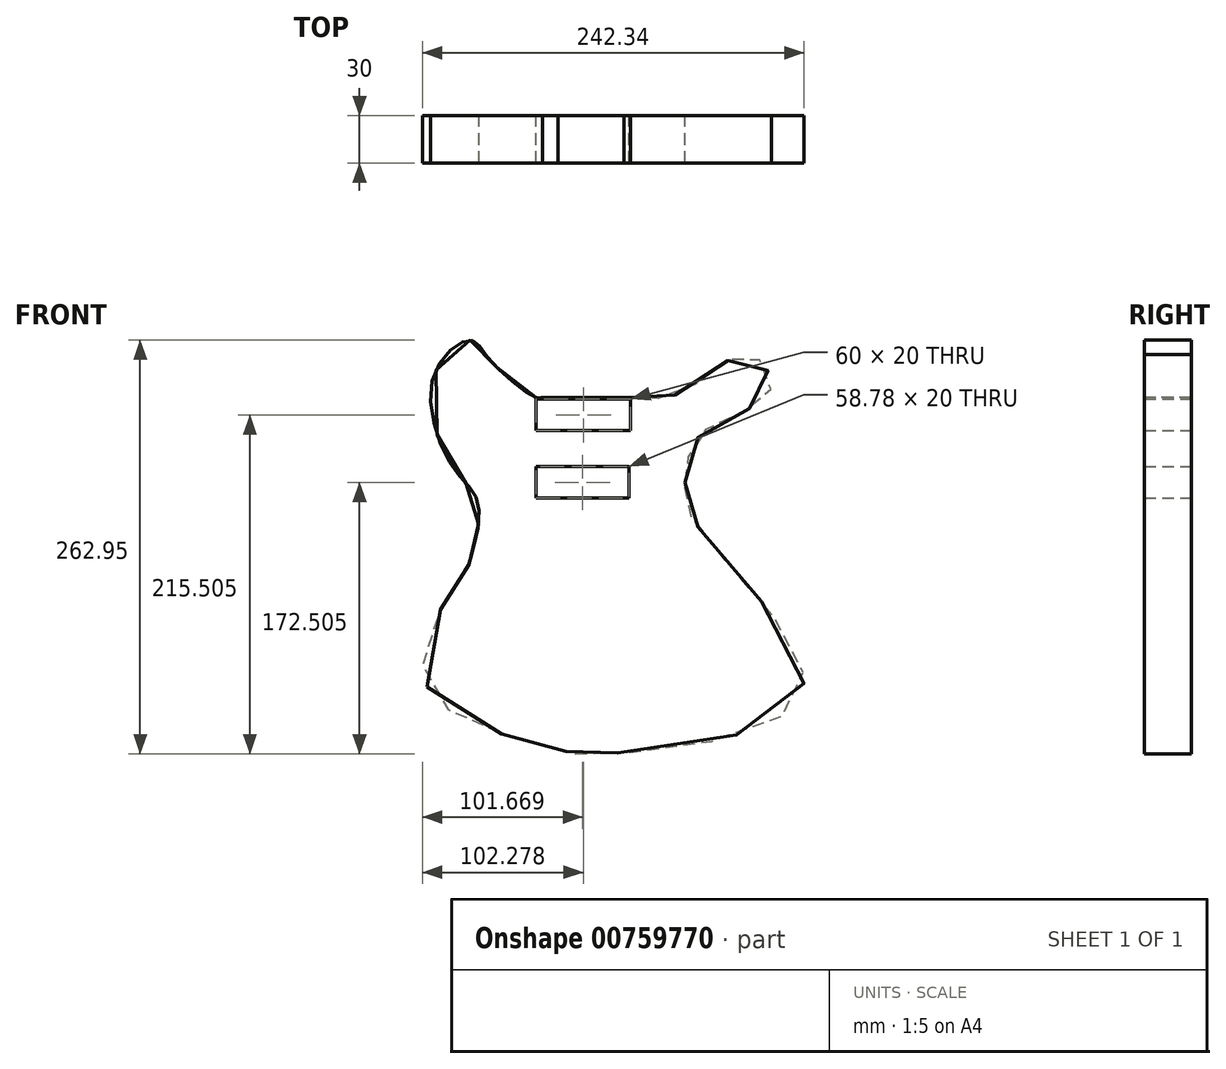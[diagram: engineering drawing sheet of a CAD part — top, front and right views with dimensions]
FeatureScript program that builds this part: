
annotation { "Feature Type Name" : "Feature", "Feature Type Description" : "" }
export const myFeature = defineFeature(function(context is Context, id is Id, definition is map)
    precondition{}
    {
        {
            var Q0;
            Q0=qCreatedBy(makeId("Front.planeOp"),FACE);
            var sketch = newSketch(context, id + "F0", { "sketchPlane" : qUnion([Q0])});
            skLineSegment(sketch, "E0", {"start": v(-20.43, 92.1) * mm, "end": v(39.57, 92.1) * mm});
            skLineSegment(sketch, "E1.bottom", {"start": v(-20.43, 91.1) * mm, "end": v(39.57, 91.1) * mm});
            skLineSegment(sketch, "E1.top", {"start": v(-20.43, 71.1) * mm, "end": v(39.57, 71.1) * mm});
            skLineSegment(sketch, "E1.left", {"start": v(-20.43, 91.1) * mm, "end": v(-20.43, 71.1) * mm});
            skLineSegment(sketch, "E1.right", {"start": v(39.57, 91.1) * mm, "end": v(39.57, 71.1) * mm});
            skLineSegment(sketch, "E2.bottom", {"start": v(-20.43, 48.1) * mm, "end": v(38.35, 48.1) * mm});
            skLineSegment(sketch, "E2.top", {"start": v(-20.43, 28.1) * mm, "end": v(38.35, 28.1) * mm});
            skLineSegment(sketch, "E2.left", {"start": v(-20.43, 48.1) * mm, "end": v(-20.43, 28.1) * mm});
            skLineSegment(sketch, "E2.right", {"start": v(38.35, 48.1) * mm, "end": v(38.35, 28.1) * mm});
            skFitSpline(sketch, "E3", {"points": [v(-20.43, 92.1) * mm, v(-50.26, 116.5) * mm, v(-62.63, 128.54) * mm, v(-85.75, 105.12) * mm, v(-72.23, 46.27) * mm, v(-56.92, 23.15) * mm, v(-62.63, -11.98) * mm, v(-64.73, -16.78) * mm, v(-90.55, -90.04) * mm, v(-3.78, -131.78) * mm, v(4.63, -134.18) * mm, v(146.95, -99.05) * mm, v(83.9, 7.54) * mm, v(74.3, 39.97) * mm, v(86.6, 71.2) * mm, v(128.04, 95.82) * mm, v(114.83, 119.24) * mm, v(70.69, 94.92) * mm, v(39.57, 92.1) * mm, v(35.24, 92.1) * mm, v(32.06, 92.1) * mm, v(25.05, 92.1) * mm, v(19.53, 92.1) * mm, v(12.84, 92.1) * mm, v(2.23, 92.1) * mm, v(-6.48, 92.1) * mm, v(-16.35, 92.1) * mm, v(-20.43, 92.1) * mm]});
            skSolve(sketch);
        }
        {
            var Q0;
            Q0=makeQuery(id+"F0.imprint","IMPRINT",FACE,{"disambiguationData":[TD([[makeQuery(id+"F0.imprint","IMPRINT",EDGE,{"derivedFrom":sQuery(id+"F0.wireOp",EDGE,"E1.bottom")}),1.0]])]});
            extrude(context, id + "F1", {"entities" : qUnion([Q0]), "depth" : 30 * mm, "offsetDistance" : 25 * mm});
        }
    });
